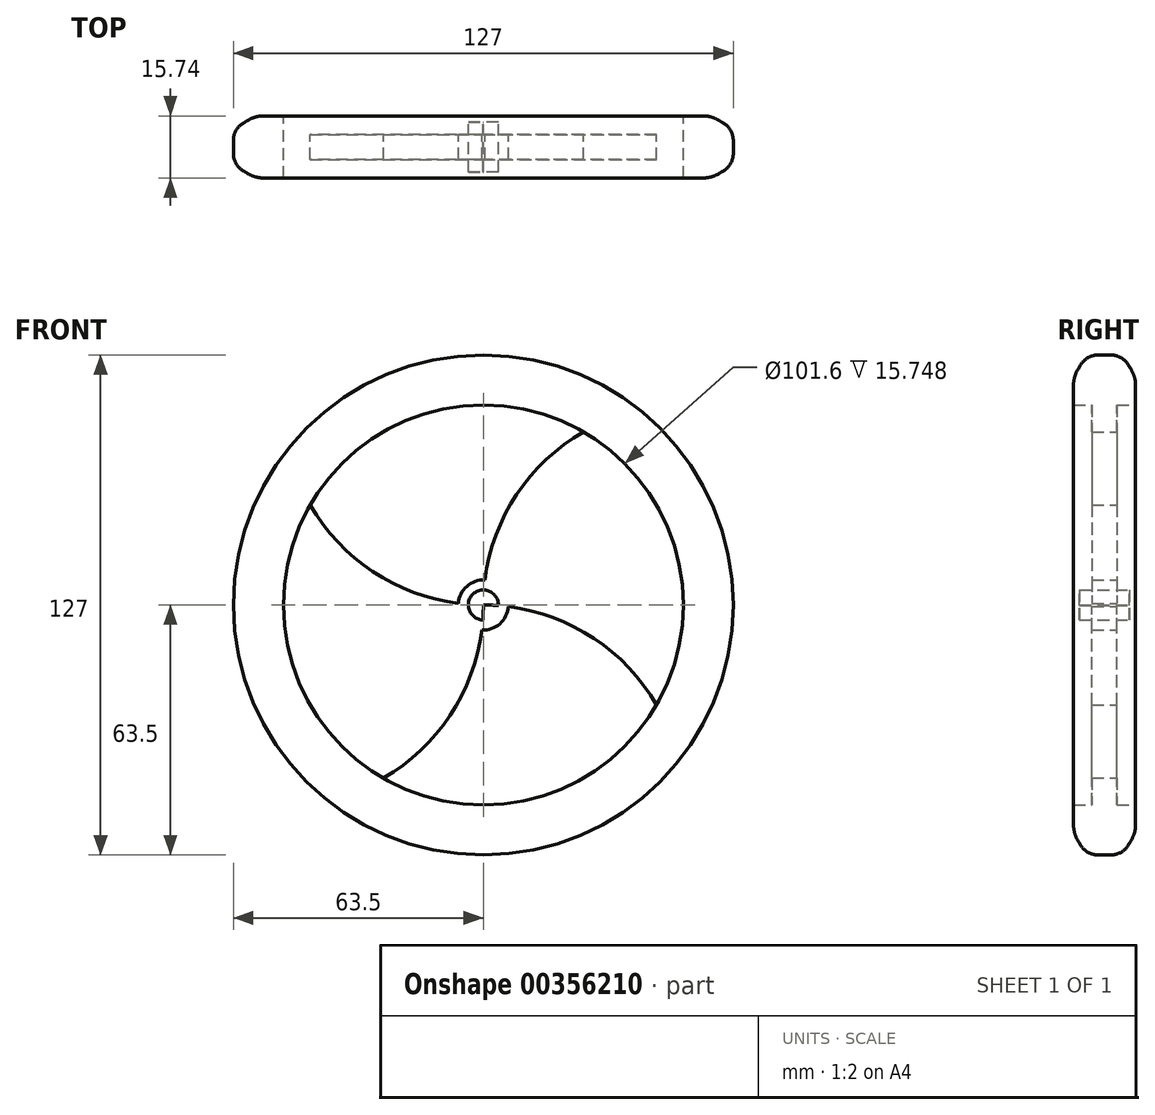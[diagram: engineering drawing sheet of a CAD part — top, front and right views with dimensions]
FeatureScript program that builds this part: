
annotation { "Feature Type Name" : "Feature", "Feature Type Description" : "" }
export const myFeature = defineFeature(function(context is Context, id is Id, definition is map)
    precondition{}
    {
        {
            var Q0;
            Q0=qCreatedBy(makeId("Front.planeOp"),FACE);
            var sketch = newSketch(context, id + "F0", { "sketchPlane" : qUnion([Q0])});
            skCircle(sketch, "E0", {"center": v(0, 0) * mm, "radius": 63.5 * mm});
            skCircle(sketch, "E1", {"center": v(0, 0) * mm, "radius": 50.8 * mm});
            skArc(sketch, "E2", {"start": v(0, 0) * mm, "mid": v(6.8, 25.4) * mm, "end": v(25.4, 44) * mm});
            skArc(sketch, "E3", {"start": v(0, 0) * mm, "mid": v(-25.4, 6.8) * mm, "end": v(-44, 25.4) * mm});
            skArc(sketch, "E4", {"start": v(0, 0) * mm, "mid": v(-6.8, -25.4) * mm, "end": v(-25.4, -44) * mm});
            skArc(sketch, "E5", {"start": v(0, 0) * mm, "mid": v(25.4, -6.8) * mm, "end": v(44, -25.4) * mm});
            skCircle(sketch, "E6", {"center": v(0, 0) * mm, "radius": 6.35 * mm});
            skCircle(sketch, "E7", {"center": v(0, 0) * mm, "radius": 3.81 * mm});
            skSolve(sketch);
        }
        {
            var Q0;
            Q0=makeQuery(id+"F0.imprint","IMPRINT",FACE,{"disambiguationData":[TD([[makeQuery(id+"F0.imprint","IMPRINT",EDGE,{"derivedFrom":sQuery(id+"F0.wireOp",EDGE,"E0")}),1.0]])]});
            extrude(context, id + "F1", {"entities" : qUnion([Q0]), "endBound" : BoundingType.SYMMETRIC, "depth" : 15.75 * mm});
        }
        {
            var Q0;
            {var subQ0=sQuery(id+"F0.wireOp",EDGE,"E4");var subQ1=sQuery(id+"F0.wireOp",EDGE,"E1");var subQ2=makeQuery(id+"F0.imprint","INTERSECT",VERTEX,{"derivedFrom":[subQ1,subQ0]});Q0=makeQuery(id+"F0.imprint","IMPRINT",FACE,{"disambiguationData":[TD([[makeQuery(id+"F0.imprint","IMPRINT",EDGE,{"disambiguationData":[TD([[subQ2,-1.0]])],"derivedFrom":subQ1}),1.0]])]});}
            var Q1;
            {var subQ0=sQuery(id+"F0.wireOp",EDGE,"E2");var subQ1=sQuery(id+"F0.wireOp",EDGE,"E1");var subQ2=makeQuery(id+"F0.imprint","INTERSECT",VERTEX,{"derivedFrom":[subQ1,subQ0]});Q1=makeQuery(id+"F0.imprint","IMPRINT",FACE,{"disambiguationData":[TD([[makeQuery(id+"F0.imprint","IMPRINT",EDGE,{"disambiguationData":[TD([[subQ2,-1.0]])],"derivedFrom":subQ1}),1.0]])]});}
            extrude(context, id + "F2", {"entities" : qUnion([Q0, Q1]), "operationType" : NewBodyOperationType.ADD, "endBound" : BoundingType.SYMMETRIC, "depth" : 6.35 * mm});
        }
        {
            var Q0;
            Q0=sQuery(id+"F0.wireOp",EDGE,"E6");
            extrude(context, id + "F3", {"bodyType" : ToolBodyType.SURFACE, "surfaceEntities" : qUnion([Q0]), "endBound" : BoundingType.SYMMETRIC, "depth" : 12.7 * mm});
        }
        {
            var Q0;
            Q0=makeQuery(id+"F1.opExtrude","CAP_EDGE",EDGE,{"disambiguationData":[OSD([sQuery(id+"F0.wireOp",EDGE,"E0")])],"isStart":true});
            var Q1;
            Q1=makeQuery(id+"F1.opExtrude","CAP_EDGE",EDGE,{"disambiguationData":[OSD([sQuery(id+"F0.wireOp",EDGE,"E0")])],"isStart":false});
            fillet(context, id + "F4", {"entities" : qUnion([Q0, Q1]), "radius" : 7.62 * mm, "tangentPropagation" : true, "allowEdgeOverflow" : false});
        }
        {
            var Q0;
            Q0 = qSketchRegion(id + "F0", true);
            var Q1;
            {var subQ0=sQuery(id+"F0.wireOp",EDGE,"E7");var subQ1=sQuery(id+"F0.wireOp",EDGE,"E2");var subQ2=makeQuery(id+"F0.imprint","INTERSECT",VERTEX,{"derivedFrom":[subQ1,subQ0]});Q1=makeQuery(id+"F0.imprint","IMPRINT",FACE,{"disambiguationData":[TD([[makeQuery(id+"F0.imprint","IMPRINT",EDGE,{"disambiguationData":[TD([[subQ2,-1.0]])],"derivedFrom":subQ1}),-1.0]])]});}
            var Q2;
            {var subQ0=sQuery(id+"F0.wireOp",EDGE,"E7");var subQ1=sQuery(id+"F0.wireOp",EDGE,"E2");var subQ2=makeQuery(id+"F0.imprint","INTERSECT",VERTEX,{"derivedFrom":[subQ1,subQ0]});Q2=makeQuery(id+"F0.imprint","IMPRINT",FACE,{"disambiguationData":[TD([[makeQuery(id+"F0.imprint","IMPRINT",EDGE,{"disambiguationData":[TD([[subQ2,-1.0]])],"derivedFrom":subQ1}),1.0]])]});}
            var Q3;
            {var subQ0=sQuery(id+"F0.wireOp",EDGE,"E7");var subQ1=sQuery(id+"F0.wireOp",EDGE,"E3");var subQ2=makeQuery(id+"F0.imprint","INTERSECT",VERTEX,{"derivedFrom":[subQ1,subQ0]});Q3=makeQuery(id+"F0.imprint","IMPRINT",FACE,{"disambiguationData":[TD([[makeQuery(id+"F0.imprint","IMPRINT",EDGE,{"disambiguationData":[TD([[subQ2,-1.0]])],"derivedFrom":subQ1}),1.0]])]});}
            var Q4;
            {var subQ0=sQuery(id+"F0.wireOp",EDGE,"E7");var subQ1=sQuery(id+"F0.wireOp",EDGE,"E4");var subQ2=makeQuery(id+"F0.imprint","INTERSECT",VERTEX,{"derivedFrom":[subQ1,subQ0]});Q4=makeQuery(id+"F0.imprint","IMPRINT",FACE,{"disambiguationData":[TD([[makeQuery(id+"F0.imprint","IMPRINT",EDGE,{"disambiguationData":[TD([[subQ2,-1.0]])],"derivedFrom":subQ1}),1.0]])]});}
            extrude(context, id + "F5", {"entities" : qUnion([Q0, Q1, Q2, Q3, Q4]), "operationType" : NewBodyOperationType.ADD, "endBound" : BoundingType.SYMMETRIC, "depth" : 12.7 * mm});
        }
        {
            var Q0;
            Q0=makeQuery(id+"F5.opExtrude","CAP_EDGE",EDGE,{"disambiguationData":[OSD([sQuery(id+"F0.wireOp",EDGE,"E0")])],"isStart":true});
            var Q1;
            Q1=makeQuery(id+"F5.opExtrude","CAP_EDGE",EDGE,{"disambiguationData":[OSD([sQuery(id+"F0.wireOp",EDGE,"E0")])],"isStart":false});
            fillet(context, id + "F6", {"entities" : qUnion([Q0, Q1]), "radius" : 5.08 * mm, "tangentPropagation" : true, "allowEdgeOverflow" : false});
        }
        {
            var Q0;
            {var subQ0=sQuery(id+"F0.wireOp",EDGE,"E0");Q0=makeQuery(id+"F6.opFillet","BLEND_EDGE",EDGE,{"blendedFrom":[makeQuery(id+"F5.opExtrude","CAP_EDGE",EDGE,{"disambiguationData":[OSD([subQ0])],"isStart":false}),makeQuery(id+"F4.opFillet","BLEND_FACE",FACE,{"disambiguationData":[OSD([subQ0]),TDD([makeQuery(id+"F1.opExtrude","CAP_EDGE",EDGE,{"disambiguationData":[OSD([subQ0])],"isStart":false})])]})],"blendedInto":[makeQuery(id+"F4.opFillet","BLEND_FACE",FACE,{"disambiguationData":[OSD([subQ0]),TDD([makeQuery(id+"F1.opExtrude","CAP_EDGE",EDGE,{"disambiguationData":[OSD([subQ0])],"isStart":false})])]})]});}
            var Q1;
            {var subQ0=sQuery(id+"F0.wireOp",EDGE,"E0");Q1=makeQuery(id+"F6.opFillet","BLEND_EDGE",EDGE,{"blendedFrom":[makeQuery(id+"F5.opExtrude","CAP_EDGE",EDGE,{"disambiguationData":[OSD([subQ0])],"isStart":true}),makeQuery(id+"F4.opFillet","BLEND_FACE",FACE,{"disambiguationData":[OSD([subQ0]),TDD([makeQuery(id+"F1.opExtrude","CAP_EDGE",EDGE,{"disambiguationData":[OSD([subQ0])],"isStart":true})])]})],"blendedInto":[makeQuery(id+"F4.opFillet","BLEND_FACE",FACE,{"disambiguationData":[OSD([subQ0]),TDD([makeQuery(id+"F1.opExtrude","CAP_EDGE",EDGE,{"disambiguationData":[OSD([subQ0])],"isStart":true})])]})]});}
            fillet(context, id + "F7", {"entities" : qUnion([Q0, Q1]), "radius" : 5.08 * mm, "tangentPropagation" : true, "allowEdgeOverflow" : false});
        }
    });
